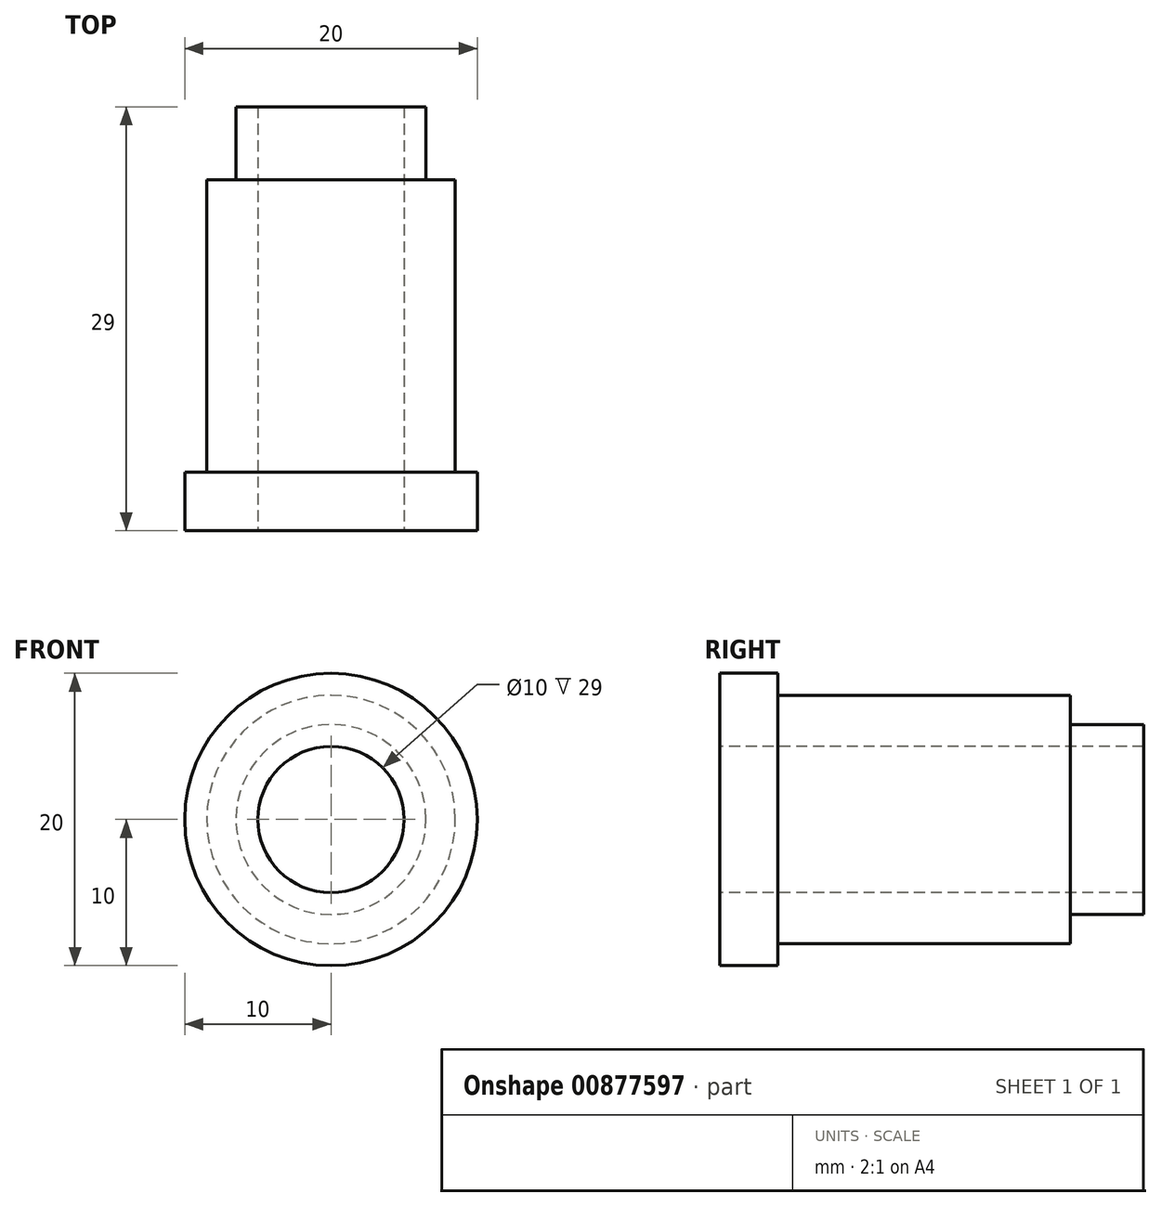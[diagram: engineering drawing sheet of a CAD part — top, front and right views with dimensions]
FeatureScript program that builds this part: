
annotation { "Feature Type Name" : "Feature", "Feature Type Description" : "" }
export const myFeature = defineFeature(function(context is Context, id is Id, definition is map)
    precondition{}
    {
        {
            var Q0;
            Q0=qCreatedBy(makeId("Right.planeOp"),FACE);
            var sketch = newSketch(context, id + "F0", { "sketchPlane" : qUnion([Q0])});
            skLineSegment(sketch, "E0", {"start": v(19, 5) * mm, "end": v(-10, 5) * mm});
            skLineSegment(sketch, "E1", {"start": v(-10, 5) * mm, "end": v(-10, 10) * mm});
            skLineSegment(sketch, "E2", {"start": v(-10, 10) * mm, "end": v(-6, 10) * mm});
            skLineSegment(sketch, "E3", {"start": v(-6, 10) * mm, "end": v(-6, 8.5) * mm});
            skLineSegment(sketch, "E4", {"start": v(-6, 8.5) * mm, "end": v(14, 8.5) * mm});
            skLineSegment(sketch, "E5", {"start": v(19, 6.5) * mm, "end": v(19, 5) * mm});
            skLineSegment(sketch, "E6", {"start": v(-24.91, 0) * mm, "end": v(32.76, 0) * mm, "construction": true});
            skLineSegment(sketch, "E7", {"start": v(19, 6.5) * mm, "end": v(14, 6.5) * mm});
            skLineSegment(sketch, "E8", {"start": v(14, 6.5) * mm, "end": v(14, 8.5) * mm});
            skPoint(sketch, "E9.orphan", {"position": v(19, 8.5) * mm});
            skSolve(sketch);
        }
        {
            var Q0;
            Q0 = qSketchRegion(id + "F0", true);
            var Q1;
            Q1=sQuery(id+"F0.wireOp",EDGE,"E6");
            revolve(context, id + "F1", {"surfaceOperationType" : NewSurfaceOperationType.NEW, "entities" : qUnion([Q0]), "axis" : qUnion([Q1]), "revolveType" : RevolveType.FULL});
        }
    });
